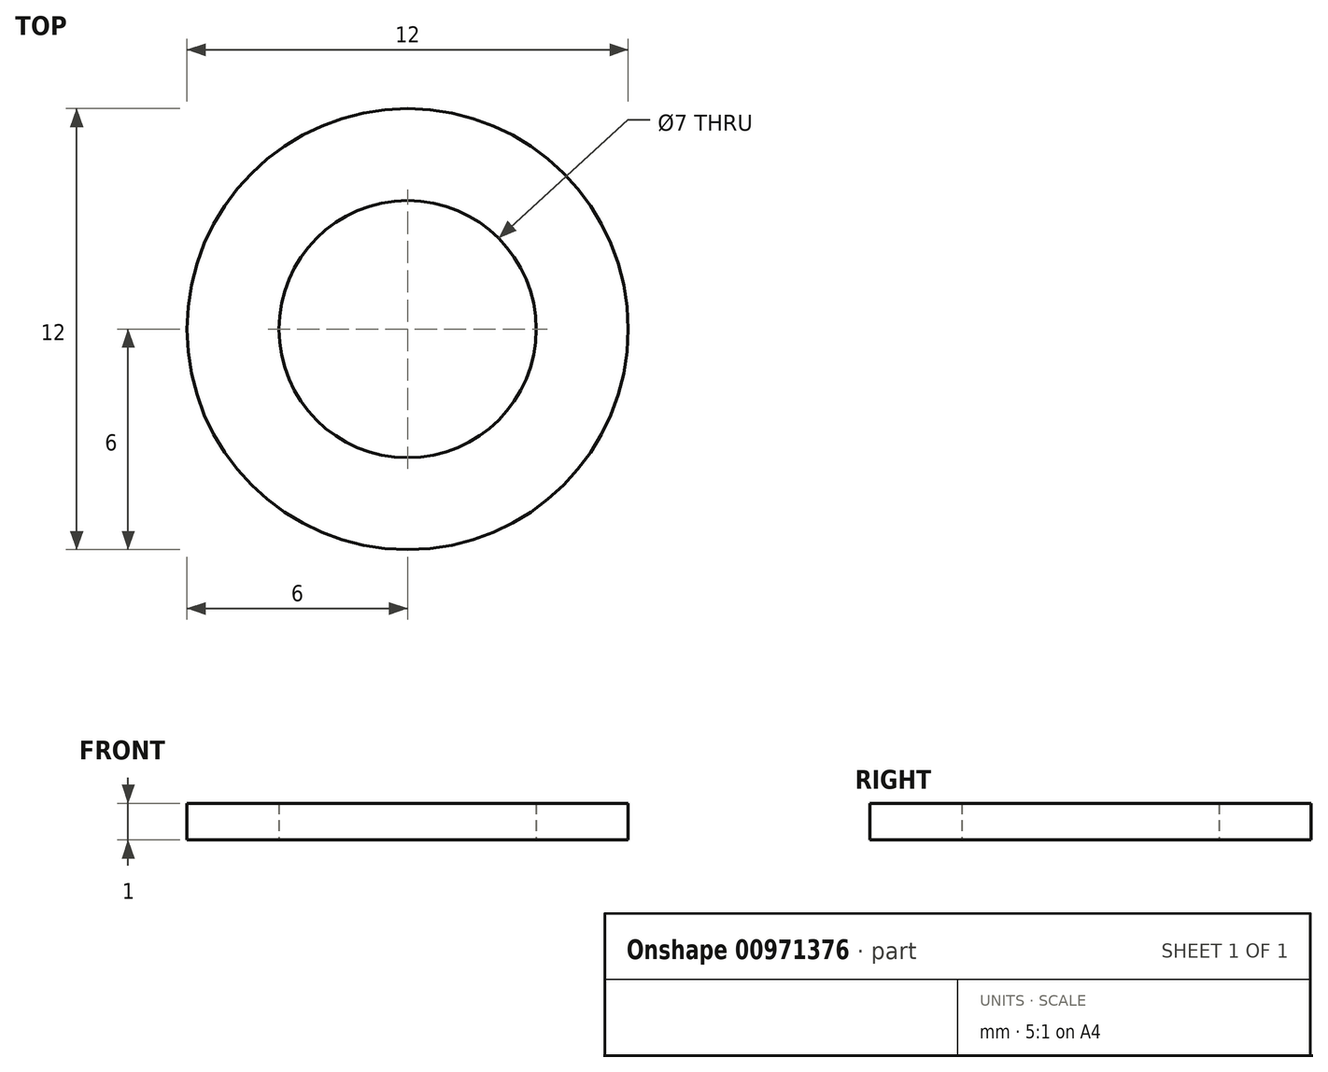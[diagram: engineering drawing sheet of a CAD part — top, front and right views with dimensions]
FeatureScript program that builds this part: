
annotation { "Feature Type Name" : "Feature", "Feature Type Description" : "" }
export const myFeature = defineFeature(function(context is Context, id is Id, definition is map)
    precondition{}
    {
        {
            var Q0;
            Q0=qCreatedBy(makeId("Top.planeOp"),FACE);
            var sketch = newSketch(context, id + "F0", { "sketchPlane" : qUnion([Q0])});
            skCircle(sketch, "E0", {"center": v(0, 0) * mm, "radius": 6 * mm});
            skCircle(sketch, "E1", {"center": v(0, 0) * mm, "radius": 3.5 * mm});
            skSolve(sketch);
        }
        {
            var Q0;
            Q0=makeQuery(id+"F0.imprint","IMPRINT",FACE,{"disambiguationData":[TD([[makeQuery(id+"F0.imprint","IMPRINT",EDGE,{"derivedFrom":sQuery(id+"F0.wireOp",EDGE,"E0")}),1.0]])]});
            extrude(context, id + "F1", {"entities" : qUnion([Q0]), "depth" : 1 * mm, "offsetDistance" : 25 * mm});
        }
    });
